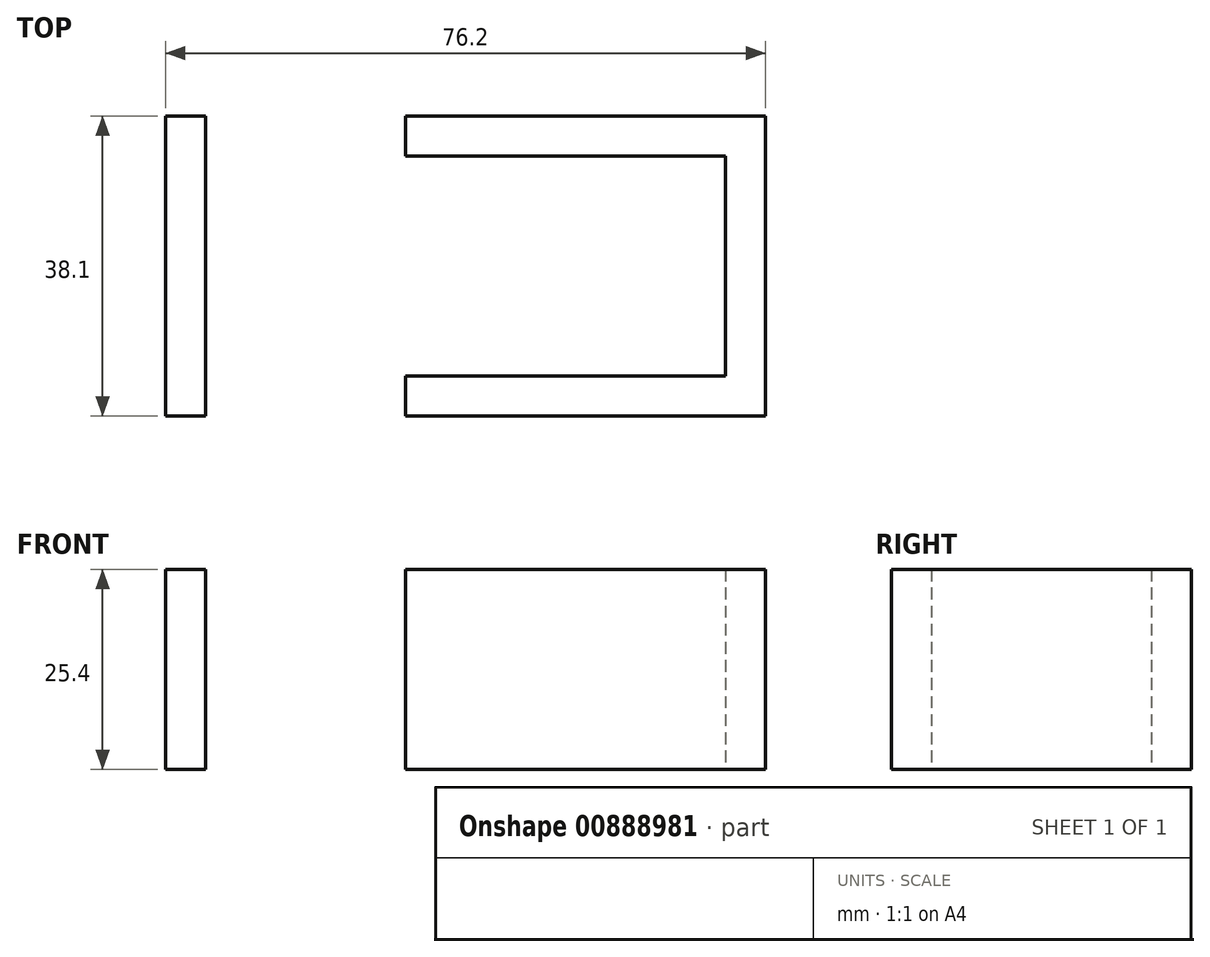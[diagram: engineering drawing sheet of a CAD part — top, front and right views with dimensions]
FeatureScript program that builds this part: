
annotation { "Feature Type Name" : "Feature", "Feature Type Description" : "" }
export const myFeature = defineFeature(function(context is Context, id is Id, definition is map)
    precondition{}
    {
        {
            var Q0;
            Q0=qCreatedBy(makeId("Top.planeOp"),FACE);
            var sketch = newSketch(context, id + "F0", { "sketchPlane" : qUnion([Q0])});
            skLineSegment(sketch, "E0.bottom", {"start": v(0, 0) * mm, "end": v(76.2, 0) * mm});
            skLineSegment(sketch, "E0.top", {"start": v(0, -38.1) * mm, "end": v(76.2, -38.1) * mm});
            skLineSegment(sketch, "E0.left", {"start": v(0, 0) * mm, "end": v(0, -38.1) * mm});
            skLineSegment(sketch, "E0.right", {"start": v(76.2, 0) * mm, "end": v(76.2, -38.1) * mm});
            skLineSegment(sketch, "E1.bottom", {"start": v(5.08, -5.08) * mm, "end": v(71.12, -5.08) * mm});
            skLineSegment(sketch, "E1.top", {"start": v(5.08, -33.02) * mm, "end": v(71.12, -33.02) * mm});
            skLineSegment(sketch, "E1.left", {"start": v(5.08, -5.08) * mm, "end": v(5.08, -33.02) * mm});
            skLineSegment(sketch, "E1.right", {"start": v(71.12, -5.08) * mm, "end": v(71.12, -33.02) * mm});
            skLineSegment(sketch, "E2.bottom", {"start": v(5.08, -33.02) * mm, "end": v(30.48, -33.02) * mm});
            skLineSegment(sketch, "E2.top", {"start": v(5.08, -38.1) * mm, "end": v(30.48, -38.1) * mm});
            skLineSegment(sketch, "E2.left", {"start": v(5.08, -33.02) * mm, "end": v(5.08, -38.1) * mm});
            skLineSegment(sketch, "E2.right", {"start": v(30.48, -33.02) * mm, "end": v(30.48, -38.1) * mm});
            skLineSegment(sketch, "E3.bottom", {"start": v(5.08, -5.08) * mm, "end": v(30.48, -5.08) * mm});
            skLineSegment(sketch, "E3.top", {"start": v(5.08, 0) * mm, "end": v(30.48, 0) * mm});
            skLineSegment(sketch, "E3.left", {"start": v(5.08, -5.08) * mm, "end": v(5.08, 0) * mm});
            skLineSegment(sketch, "E3.right", {"start": v(30.48, -5.08) * mm, "end": v(30.48, 0) * mm});
            skSolve(sketch);
        }
        {
            var Q0;
            {var subQ0=sQuery(id+"F0.wireOp",EDGE,"E0.left");Q0=makeQuery(id+"F0.imprint","IMPRINT",FACE,{"disambiguationData":[TD([[makeQuery(id+"F0.imprint","IMPRINT",EDGE,{"derivedFrom":subQ0}),1.0]])]});}
            var Q1;
            {var subQ0=sQuery(id+"F0.wireOp",EDGE,"E0.right");Q1=makeQuery(id+"F0.imprint","IMPRINT",FACE,{"disambiguationData":[TD([[makeQuery(id+"F0.imprint","IMPRINT",EDGE,{"derivedFrom":subQ0}),-1.0]])]});}
            extrude(context, id + "F1", {"entities" : qUnion([Q0, Q1]), "depth" : 25.4 * mm, "offsetDistance" : 25.4 * mm});
        }
    });
